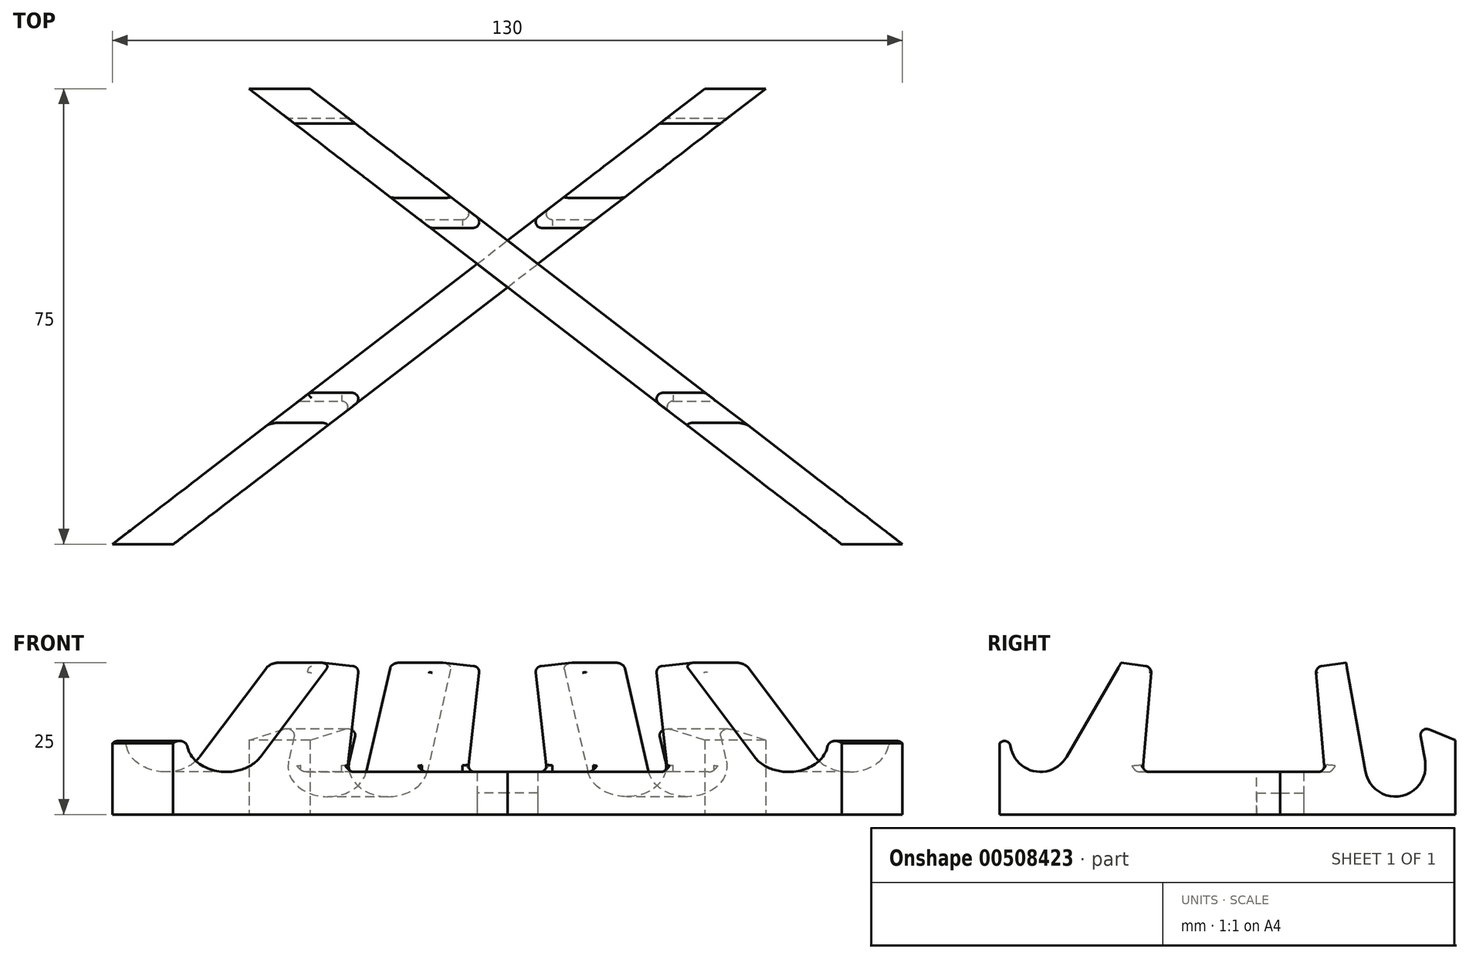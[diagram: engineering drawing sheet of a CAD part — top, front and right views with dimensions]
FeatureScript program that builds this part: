
annotation { "Feature Type Name" : "Feature", "Feature Type Description" : "" }
export const myFeature = defineFeature(function(context is Context, id is Id, definition is map)
    precondition{}
    {
        {
            var Q0;
            Q0=qCreatedBy(makeId("Top.planeOp"),FACE);
            var sketch = newSketch(context, id + "F0", { "sketchPlane" : qUnion([Q0])});
            skLineSegment(sketch, "E0.bottom", {"start": v(-55, 0) * mm, "end": v(-65, 0) * mm});
            skLineSegment(sketch, "E0.top", {"start": v(42.5, 75) * mm, "end": v(32.5, 75) * mm});
            skLineSegment(sketch, "E0.left", {"start": v(-55, 0) * mm, "end": v(42.5, 75) * mm});
            skLineSegment(sketch, "E0.right", {"start": v(-65, 0) * mm, "end": v(32.5, 75) * mm});
            skLineSegment(sketch, "E1", {"start": v(0, -60.62) * mm, "end": v(0, 193.14) * mm, "construction": true});
            skPoint(sketch, "E2", {"position": v(0, 50) * mm});
            skLineSegment(sketch, "E3.MirrorCS", {"start": v(65, 0) * mm, "end": v(-32.5, 75) * mm});
            skLineSegment(sketch, "E4.MirrorCS", {"start": v(55, 0) * mm, "end": v(-42.5, 75) * mm});
            skLineSegment(sketch, "E5.MirrorCS", {"start": v(-42.5, 75) * mm, "end": v(-32.5, 75) * mm});
            skLineSegment(sketch, "E6.MirrorCS", {"start": v(55, 0) * mm, "end": v(65, 0) * mm});
            skSolve(sketch);
        }
        {
            var Q0;
            {var subQ0=sQuery(id+"F0.wireOp",EDGE,"E0.bottom");Q0=makeQuery(id+"F0.imprint","IMPRINT",FACE,{"disambiguationData":[TD([[makeQuery(id+"F0.imprint","IMPRINT",EDGE,{"derivedFrom":subQ0}),-1.0]])]});}
            var Q1;
            {var subQ0=sQuery(id+"F0.wireOp",EDGE,"E4.MirrorCS");var subQ1=sQuery(id+"F0.wireOp",EDGE,"E0.left");var subQ2=makeQuery(id+"F0.imprint","INTERSECT",VERTEX,{"derivedFrom":[subQ1,subQ0]});Q1=makeQuery(id+"F0.imprint","IMPRINT",FACE,{"disambiguationData":[TD([[makeQuery(id+"F0.imprint","IMPRINT",EDGE,{"disambiguationData":[TD([[subQ2,-1.0]])],"derivedFrom":subQ1}),1.0]])]});}
            var Q2;
            {var subQ0=sQuery(id+"F0.wireOp",EDGE,"E0.top");Q2=makeQuery(id+"F0.imprint","IMPRINT",FACE,{"disambiguationData":[TD([[makeQuery(id+"F0.imprint","IMPRINT",EDGE,{"derivedFrom":subQ0}),1.0]])]});}
            extrude(context, id + "F1", {"entities" : qUnion([Q0, Q1, Q2]), "depth" : 25 * mm});
        }
        {
            var Q0;
            {var subQ5=sQuery(id+"F0.wireOp",EDGE,"E6.MirrorCS");Q0=makeQuery(id+"F0.imprint","IMPRINT",FACE,{"disambiguationData":[TD([[makeQuery(id+"F0.imprint","IMPRINT",EDGE,{"derivedFrom":subQ5}),1.0]])]});}
            var Q1;
            {var subQ5=sQuery(id+"F0.wireOp",EDGE,"E5.MirrorCS");Q1=makeQuery(id+"F0.imprint","IMPRINT",FACE,{"disambiguationData":[TD([[makeQuery(id+"F0.imprint","IMPRINT",EDGE,{"derivedFrom":subQ5}),-1.0]])]});}
            var Q2;
            {var subQ0=sQuery(id+"F0.wireOp",EDGE,"E4.MirrorCS");var subQ1=sQuery(id+"F0.wireOp",EDGE,"E0.left");var subQ2=makeQuery(id+"F0.imprint","INTERSECT",VERTEX,{"derivedFrom":[subQ1,subQ0]});Q2=makeQuery(id+"F0.imprint","IMPRINT",FACE,{"disambiguationData":[TD([[makeQuery(id+"F0.imprint","IMPRINT",EDGE,{"disambiguationData":[TD([[subQ2,-1.0]])],"derivedFrom":subQ1}),1.0]])]});}
            extrude(context, id + "F2", {"entities" : qUnion([Q0, Q1, Q2]), "depth" : 25 * mm});
        }
        {
            var Q0;
            Q0=qCreatedBy(makeId("Right.planeOp"),FACE);
            var sketch = newSketch(context, id + "F3", { "sketchPlane" : qUnion([Q0])});
            skLineSegment(sketch, "E7", {"start": v(3.4, 16.23) * mm, "end": v(0, 11.72) * mm});
            skLineSegment(sketch, "E8", {"start": v(3.4, 16.23) * mm, "end": v(2.4, 14.5) * mm});
            skLineSegment(sketch, "E9", {"start": v(2.4, 14.5) * mm, "end": v(11.05, 9.5) * mm, "construction": true});
            skLineSegment(sketch, "E10", {"start": v(11.05, 9.5) * mm, "end": v(20, 25) * mm});
            skLineSegment(sketch, "E11", {"start": v(75, 7) * mm, "end": v(75, 25) * mm, "construction": true});
            skLineSegment(sketch, "E12", {"start": v(75, 25) * mm, "end": v(0, 25) * mm});
            skLineSegment(sketch, "E13", {"start": v(0, 25) * mm, "end": v(0, 11.72) * mm});
            skArc(sketch, "E14", {"start": v(2.4, 14.5) * mm, "mid": v(4.22, 7.67) * mm, "end": v(11.05, 9.5) * mm});
            skLineSegment(sketch, "E15", {"start": v(20, 25) * mm, "end": v(25, 24.3) * mm});
            skLineSegment(sketch, "E16", {"start": v(25, 24.3) * mm, "end": v(23.49, 7) * mm});
            skLineSegment(sketch, "E17", {"start": v(23.49, 7) * mm, "end": v(75, 7) * mm, "construction": true});
            skLineSegment(sketch, "E18", {"start": v(57, 25) * mm, "end": v(52, 24.3) * mm});
            skLineSegment(sketch, "E19", {"start": v(52, 24.3) * mm, "end": v(53.51, 7) * mm});
            skLineSegment(sketch, "E20", {"start": v(23.49, 7) * mm, "end": v(53.51, 7) * mm});
            skLineSegment(sketch, "E21", {"start": v(57, 25) * mm, "end": v(60.16, 7.06) * mm});
            skArc(sketch, "E22", {"start": v(60.16, 7.06) * mm, "mid": v(65.96, 3) * mm, "end": v(70.01, 8.8) * mm});
            skLineSegment(sketch, "E23", {"start": v(70.01, 8.8) * mm, "end": v(60.16, 7.06) * mm, "construction": true});
            skLineSegment(sketch, "E24", {"start": v(75, 25) * mm, "end": v(75, 12.21) * mm});
            skLineSegment(sketch, "E25", {"start": v(75, 12.21) * mm, "end": v(68.97, 14.7) * mm});
            skLineSegment(sketch, "E26", {"start": v(68.97, 14.7) * mm, "end": v(70.01, 8.8) * mm});
            skSolve(sketch);
        }
        {
            var Q0;
            Q0=qSketchRegion(id+"F3",true);
            extrude(context, id + "F4", {"entities" : qUnion([Q0]), "operationType" : NewBodyOperationType.REMOVE, "endBound" : BoundingType.THROUGH_ALL, "depth" : 25 * mm, "hasSecondDirection" : true, "secondDirectionBound" : BoundingType.THROUGH_ALL, "secondDirectionOppositeDirection" : true, "secondDirectionDepth" : 25 * mm});
        }
        {
            var Q0;
            {var subQ0=sQuery(id+"F0.wireOp",EDGE,"E4.MirrorCS");var subQ1=sQuery(id+"F0.wireOp",EDGE,"E0.left");var subQ2=makeQuery(id+"F0.imprint","INTERSECT",VERTEX,{"derivedFrom":[subQ1,subQ0]});Q0=makeQuery(id+"F0.imprint","IMPRINT",FACE,{"disambiguationData":[TD([[makeQuery(id+"F0.imprint","IMPRINT",EDGE,{"disambiguationData":[TD([[subQ2,-1.0]])],"derivedFrom":subQ1}),1.0]])]});}
            extrude(context, id + "F5", {"entities" : qUnion([Q0]), "operationType" : NewBodyOperationType.REMOVE, "depth" : 3.5 * mm});
        }
        {
            var Q0;
            Q0=makeQuery(id+"F2.opExtrude","SWEPT_BODY",BODY,{"disambiguationData":[OSD([sQuery(id+"F0.wireOp",EDGE,"E3.MirrorCS"),sQuery(id+"F0.wireOp",EDGE,"E4.MirrorCS"),sQuery(id+"F0.wireOp",EDGE,"E5.MirrorCS"),sQuery(id+"F0.wireOp",EDGE,"E6.MirrorCS")])]});
            var Q1;
            Q1=makeQuery(id+"F1.opExtrude","SWEPT_BODY",BODY,{"disambiguationData":[OSD([sQuery(id+"F0.wireOp",EDGE,"E0.bottom"),sQuery(id+"F0.wireOp",EDGE,"E0.top"),sQuery(id+"F0.wireOp",EDGE,"E0.left"),sQuery(id+"F0.wireOp",EDGE,"E0.right")])]});
            booleanBodies(context, id + "F6", {"operationType" : BooleanOperationType.SUBTRACTION, "tools" : qUnion([Q0]), "targets" : qUnion([Q1]), "keepTools" : true});
        }
        {
            var Q0;
            Q0=makeQuery(id+"F4.boolean.opBoolean","INTERSECT",EDGE,{"derivedFrom":[makeQuery(id+"F1.opExtrude","SWEPT_FACE",FACE,{"disambiguationData":[OSD([sQuery(id+"F0.wireOp",EDGE,"E0.left")])]}),makeQuery(id+"F4.opExtrude","SWEPT_FACE",FACE,{"disambiguationData":[OSD([sQuery(id+"F3.wireOp",EDGE,"E16")])]})]});
            var Q1;
            Q1=makeQuery(id+"F4.boolean.opBoolean","INTERSECT",EDGE,{"derivedFrom":[makeQuery(id+"F2.opExtrude","SWEPT_FACE",FACE,{"disambiguationData":[OSD([sQuery(id+"F0.wireOp",EDGE,"E4.MirrorCS")])]}),makeQuery(id+"F4.opExtrude","SWEPT_FACE",FACE,{"disambiguationData":[OSD([sQuery(id+"F3.wireOp",EDGE,"E16")])]})]});
            var Q2;
            Q2=makeQuery(id+"F4.boolean.opBoolean","INTERSECT",EDGE,{"derivedFrom":[makeQuery(id+"F1.opExtrude","SWEPT_FACE",FACE,{"disambiguationData":[OSD([sQuery(id+"F0.wireOp",EDGE,"E0.right")])]}),makeQuery(id+"F4.opExtrude","SWEPT_FACE",FACE,{"disambiguationData":[OSD([sQuery(id+"F3.wireOp",EDGE,"E16")])]})]});
            var Q3;
            Q3=makeQuery(id+"F4.boolean.opBoolean","INTERSECT",EDGE,{"derivedFrom":[makeQuery(id+"F2.opExtrude","SWEPT_FACE",FACE,{"disambiguationData":[OSD([sQuery(id+"F0.wireOp",EDGE,"E3.MirrorCS")])]}),makeQuery(id+"F4.opExtrude","SWEPT_FACE",FACE,{"disambiguationData":[OSD([sQuery(id+"F3.wireOp",EDGE,"E16")])]})]});
            var Q4;
            Q4=makeQuery(id+"F4.boolean.opBoolean","INTERSECT",EDGE,{"derivedFrom":[makeQuery(id+"F2.opExtrude","SWEPT_FACE",FACE,{"disambiguationData":[OSD([sQuery(id+"F0.wireOp",EDGE,"E4.MirrorCS")])]}),makeQuery(id+"F4.opExtrude","SWEPT_FACE",FACE,{"disambiguationData":[OSD([sQuery(id+"F3.wireOp",EDGE,"E19")])]})]});
            var Q5;
            Q5=makeQuery(id+"F4.boolean.opBoolean","INTERSECT",EDGE,{"derivedFrom":[makeQuery(id+"F2.opExtrude","SWEPT_FACE",FACE,{"disambiguationData":[OSD([sQuery(id+"F0.wireOp",EDGE,"E3.MirrorCS")])]}),makeQuery(id+"F4.opExtrude","SWEPT_FACE",FACE,{"disambiguationData":[OSD([sQuery(id+"F3.wireOp",EDGE,"E19")])]})]});
            var Q6;
            Q6=makeQuery(id+"F4.boolean.opBoolean","INTERSECT",EDGE,{"derivedFrom":[makeQuery(id+"F1.opExtrude","SWEPT_FACE",FACE,{"disambiguationData":[OSD([sQuery(id+"F0.wireOp",EDGE,"E0.right")])]}),makeQuery(id+"F4.opExtrude","SWEPT_FACE",FACE,{"disambiguationData":[OSD([sQuery(id+"F3.wireOp",EDGE,"E19")])]})]});
            var Q7;
            Q7=makeQuery(id+"F4.boolean.opBoolean","INTERSECT",EDGE,{"derivedFrom":[makeQuery(id+"F1.opExtrude","SWEPT_FACE",FACE,{"disambiguationData":[OSD([sQuery(id+"F0.wireOp",EDGE,"E0.left")])]}),makeQuery(id+"F4.opExtrude","SWEPT_FACE",FACE,{"disambiguationData":[OSD([sQuery(id+"F3.wireOp",EDGE,"E19")])]})]});
            fillet(context, id + "F7", {"entities" : qUnion([Q0, Q1, Q2, Q3, Q4, Q5, Q6, Q7]), "radius" : 1 * mm, "tangentPropagation" : true, "allowEdgeOverflow" : false});
        }
        {
            var Q0;
            {var subQ0=sQuery(id+"F0.wireOp",EDGE,"E0.left");var subQ1=sQuery(id+"F0.wireOp",EDGE,"E0.bottom");var subQ4=sQuery(id+"F3.wireOp",EDGE,"E8");var subQ5=sQuery(id+"F3.wireOp",EDGE,"E7");Q0=makeQuery(id+"F4.boolean.opBoolean","COPY",EDGE,{"disambiguationData":[TD([makeQuery(id+"F1.opExtrude","SWEPT_FACE",FACE,{"disambiguationData":[OSD([subQ0]),TDD([makeQuery(id+"F0.imprint","IMPRINT",EDGE,{"disambiguationData":[TD([[makeQuery(id+"F0.imprint","INTERSECT",VERTEX,{"derivedFrom":[subQ1,subQ0]}),-1.0]])],"derivedFrom":subQ0})])]})])],"derivedFrom":makeQuery(id+"F4.opExtrude","SWEPT_EDGE",EDGE,{"disambiguationData":[OSD([subQ5,subQ4])]})});}
            var Q1;
            {var subQ0=sQuery(id+"F0.wireOp",EDGE,"E6.MirrorCS");var subQ1=sQuery(id+"F0.wireOp",EDGE,"E3.MirrorCS");var subQ3=sQuery(id+"F3.wireOp",EDGE,"E7");var subQ5=sQuery(id+"F3.wireOp",EDGE,"E8");Q1=makeQuery(id+"F4.boolean.opBoolean","COPY",EDGE,{"disambiguationData":[TD([makeQuery(id+"F1.opExtrude","SWEPT_FACE",FACE,{"disambiguationData":[OSD([subQ1]),TDD([makeQuery(id+"F0.imprint","IMPRINT",EDGE,{"disambiguationData":[TD([[makeQuery(id+"F0.imprint","INTERSECT",VERTEX,{"derivedFrom":[subQ1,subQ0]}),-1.0]])],"derivedFrom":subQ1})])]})])],"derivedFrom":makeQuery(id+"F4.opExtrude","SWEPT_EDGE",EDGE,{"disambiguationData":[OSD([subQ3,subQ5])]})});}
            var Q2;
            {var subQ0=sQuery(id+"F3.wireOp",EDGE,"E7");Q2=makeQuery(id+"F4.boolean.opBoolean","COPY",EDGE,{"disambiguationData":[topologyDisambiguationEdgeConnected([makeQuery(id+"F1.opExtrude","SWEPT_FACE",FACE,{"disambiguationData":[OSD([sQuery(id+"F0.wireOp",EDGE,"E0.bottom")])]})])],"derivedFrom":makeQuery(id+"F4.opExtrude","SWEPT_EDGE",EDGE,{"disambiguationData":[OSD([subQ0,sQuery(id+"F3.wireOp",EDGE,"E13")])]})});}
            var Q3;
            {var subQ0=sQuery(id+"F3.wireOp",EDGE,"E7");Q3=makeQuery(id+"F4.boolean.opBoolean","COPY",EDGE,{"disambiguationData":[topologyDisambiguationEdgeConnected([makeQuery(id+"F1.opExtrude","SWEPT_FACE",FACE,{"disambiguationData":[OSD([sQuery(id+"F0.wireOp",EDGE,"E6.MirrorCS")])]})])],"derivedFrom":makeQuery(id+"F4.opExtrude","SWEPT_EDGE",EDGE,{"disambiguationData":[OSD([subQ0,sQuery(id+"F3.wireOp",EDGE,"E13")])]})});}
            var Q4;
            {var subQ0=sQuery(id+"F3.wireOp",EDGE,"E15");var subQ1=sQuery(id+"F3.wireOp",EDGE,"E12");var subQ2=sQuery(id+"F3.wireOp",EDGE,"E10");Q4=makeQuery(id+"F4.boolean.opBoolean","TWEAK_EDGE",EDGE,{"disambiguationData":[OD(0.0)],"derivedFrom":[makeQuery(id+"F4.opExtrude","SWEPT_EDGE",EDGE,{"disambiguationData":[OSD([subQ2,subQ1,subQ0]),ownerDisambiguation([makeQuery(id+"F3.imprint","IMPRINT",EDGE,{"derivedFrom":sQuery(id+"F3.wireOp",EDGE,"E7")})])]}),makeQuery(id+"F4.opExtrude","SWEPT_EDGE",EDGE,{"disambiguationData":[OSD([subQ2,subQ1,subQ0]),ownerDisambiguation([makeQuery(id+"F3.imprint","IMPRINT",EDGE,{"derivedFrom":sQuery(id+"F3.wireOp",EDGE,"E11")})])]})]});}
            var Q5;
            {var subQ0=sQuery(id+"F3.wireOp",EDGE,"E15");var subQ1=sQuery(id+"F3.wireOp",EDGE,"E12");var subQ2=sQuery(id+"F3.wireOp",EDGE,"E10");Q5=makeQuery(id+"F4.boolean.opBoolean","TWEAK_EDGE",EDGE,{"disambiguationData":[OD(1.0)],"derivedFrom":[makeQuery(id+"F4.opExtrude","SWEPT_EDGE",EDGE,{"disambiguationData":[OSD([subQ2,subQ1,subQ0]),ownerDisambiguation([makeQuery(id+"F3.imprint","IMPRINT",EDGE,{"derivedFrom":sQuery(id+"F3.wireOp",EDGE,"E7")})])]}),makeQuery(id+"F4.opExtrude","SWEPT_EDGE",EDGE,{"disambiguationData":[OSD([subQ2,subQ1,subQ0]),ownerDisambiguation([makeQuery(id+"F3.imprint","IMPRINT",EDGE,{"derivedFrom":sQuery(id+"F3.wireOp",EDGE,"E11")})])]})]});}
            var Q6;
            {var subQ0=sQuery(id+"F0.wireOp",EDGE,"E0.left");var subQ1=sQuery(id+"F0.wireOp",EDGE,"E0.bottom");var subQ4=sQuery(id+"F3.wireOp",EDGE,"E16");var subQ5=sQuery(id+"F3.wireOp",EDGE,"E15");Q6=makeQuery(id+"F4.boolean.opBoolean","COPY",EDGE,{"disambiguationData":[TD([makeQuery(id+"F1.opExtrude","SWEPT_FACE",FACE,{"disambiguationData":[OSD([subQ0]),TDD([makeQuery(id+"F0.imprint","IMPRINT",EDGE,{"disambiguationData":[TD([[makeQuery(id+"F0.imprint","INTERSECT",VERTEX,{"derivedFrom":[subQ1,subQ0]}),-1.0]])],"derivedFrom":subQ0})])]})])],"derivedFrom":makeQuery(id+"F4.opExtrude","SWEPT_EDGE",EDGE,{"disambiguationData":[OSD([subQ5,subQ4])]})});}
            var Q7;
            {var subQ0=sQuery(id+"F0.wireOp",EDGE,"E0.left");var subQ1=sQuery(id+"F0.wireOp",EDGE,"E0.bottom");var subQ4=sQuery(id+"F3.wireOp",EDGE,"E16");var subQ5=sQuery(id+"F3.wireOp",EDGE,"E17");Q7=makeQuery(id+"F4.boolean.opBoolean","COPY",EDGE,{"disambiguationData":[TD([makeQuery(id+"F1.opExtrude","SWEPT_FACE",FACE,{"disambiguationData":[OSD([subQ0]),TDD([makeQuery(id+"F0.imprint","IMPRINT",EDGE,{"disambiguationData":[TD([[makeQuery(id+"F0.imprint","INTERSECT",VERTEX,{"derivedFrom":[subQ1,subQ0]}),-1.0]])],"derivedFrom":subQ0})])]})])],"derivedFrom":makeQuery(id+"F4.opExtrude","SWEPT_EDGE",EDGE,{"disambiguationData":[OSD([subQ4,subQ5])]})});}
            var Q8;
            {var subQ0=sQuery(id+"F0.wireOp",EDGE,"E6.MirrorCS");var subQ1=sQuery(id+"F0.wireOp",EDGE,"E3.MirrorCS");var subQ4=sQuery(id+"F3.wireOp",EDGE,"E16");var subQ5=sQuery(id+"F3.wireOp",EDGE,"E17");Q8=makeQuery(id+"F4.boolean.opBoolean","COPY",EDGE,{"disambiguationData":[TD([makeQuery(id+"F1.opExtrude","SWEPT_FACE",FACE,{"disambiguationData":[OSD([subQ1]),TDD([makeQuery(id+"F0.imprint","IMPRINT",EDGE,{"disambiguationData":[TD([[makeQuery(id+"F0.imprint","INTERSECT",VERTEX,{"derivedFrom":[subQ1,subQ0]}),-1.0]])],"derivedFrom":subQ1})])]})])],"derivedFrom":makeQuery(id+"F4.opExtrude","SWEPT_EDGE",EDGE,{"disambiguationData":[OSD([subQ4,subQ5])]})});}
            var Q9;
            {var subQ0=sQuery(id+"F0.wireOp",EDGE,"E6.MirrorCS");var subQ1=sQuery(id+"F0.wireOp",EDGE,"E3.MirrorCS");var subQ4=sQuery(id+"F3.wireOp",EDGE,"E15");var subQ5=sQuery(id+"F3.wireOp",EDGE,"E16");Q9=makeQuery(id+"F4.boolean.opBoolean","COPY",EDGE,{"disambiguationData":[TD([makeQuery(id+"F1.opExtrude","SWEPT_FACE",FACE,{"disambiguationData":[OSD([subQ1]),TDD([makeQuery(id+"F0.imprint","IMPRINT",EDGE,{"disambiguationData":[TD([[makeQuery(id+"F0.imprint","INTERSECT",VERTEX,{"derivedFrom":[subQ1,subQ0]}),-1.0]])],"derivedFrom":subQ1})])]})])],"derivedFrom":makeQuery(id+"F4.opExtrude","SWEPT_EDGE",EDGE,{"disambiguationData":[OSD([subQ4,subQ5])]})});}
            var Q10;
            {var subQ0=sQuery(id+"F3.wireOp",EDGE,"E7");var subQ1=sQuery(id+"F3.wireOp",EDGE,"E8");Q10=makeQuery(id+"F4.boolean.opBoolean","COPY",EDGE,{"disambiguationData":[TD([makeQuery(id+"F2.opExtrude","SWEPT_FACE",FACE,{"disambiguationData":[OSD([sQuery(id+"F0.wireOp",EDGE,"E3.MirrorCS")])]})])],"derivedFrom":makeQuery(id+"F4.opExtrude","SWEPT_EDGE",EDGE,{"disambiguationData":[OSD([subQ0,subQ1])]})});}
            var Q11;
            {var subQ0=sQuery(id+"F3.wireOp",EDGE,"E15");var subQ1=sQuery(id+"F3.wireOp",EDGE,"E16");Q11=makeQuery(id+"F4.boolean.opBoolean","COPY",EDGE,{"disambiguationData":[TD([makeQuery(id+"F2.opExtrude","SWEPT_FACE",FACE,{"disambiguationData":[OSD([sQuery(id+"F0.wireOp",EDGE,"E3.MirrorCS")])]})])],"derivedFrom":makeQuery(id+"F4.opExtrude","SWEPT_EDGE",EDGE,{"disambiguationData":[OSD([subQ0,subQ1])]})});}
            var Q12;
            {var subQ0=sQuery(id+"F3.wireOp",EDGE,"E16");var subQ1=sQuery(id+"F3.wireOp",EDGE,"E17");Q12=makeQuery(id+"F4.boolean.opBoolean","COPY",EDGE,{"disambiguationData":[TD([makeQuery(id+"F2.opExtrude","SWEPT_FACE",FACE,{"disambiguationData":[OSD([sQuery(id+"F0.wireOp",EDGE,"E3.MirrorCS")])]})])],"derivedFrom":makeQuery(id+"F4.opExtrude","SWEPT_EDGE",EDGE,{"disambiguationData":[OSD([subQ0,subQ1])]})});}
            var Q13;
            {var subQ0=sQuery(id+"F3.wireOp",EDGE,"E19");var subQ1=sQuery(id+"F3.wireOp",EDGE,"E20");Q13=makeQuery(id+"F4.boolean.opBoolean","COPY",EDGE,{"disambiguationData":[TD([makeQuery(id+"F2.opExtrude","SWEPT_FACE",FACE,{"disambiguationData":[OSD([sQuery(id+"F0.wireOp",EDGE,"E3.MirrorCS")])]})])],"derivedFrom":makeQuery(id+"F4.opExtrude","SWEPT_EDGE",EDGE,{"disambiguationData":[OSD([subQ0,subQ1])]})});}
            var Q14;
            {var subQ0=sQuery(id+"F3.wireOp",EDGE,"E19");var subQ1=sQuery(id+"F3.wireOp",EDGE,"E20");Q14=makeQuery(id+"F4.boolean.opBoolean","COPY",EDGE,{"disambiguationData":[TD([makeQuery(id+"F1.opExtrude","SWEPT_FACE",FACE,{"disambiguationData":[OSD([sQuery(id+"F0.wireOp",EDGE,"E0.left")])]})])],"derivedFrom":makeQuery(id+"F4.opExtrude","SWEPT_EDGE",EDGE,{"disambiguationData":[OSD([subQ0,subQ1])]})});}
            var Q15;
            {var subQ0=makeQuery(id+"F1.opExtrude","SWEPT_FACE",FACE,{"disambiguationData":[OSD([sQuery(id+"F0.wireOp",EDGE,"E0.right")])]});var subQ1=makeQuery(id+"F4.opExtrude","SWEPT_FACE",FACE,{"disambiguationData":[OSD([sQuery(id+"F3.wireOp",EDGE,"E19")])]});Q15=makeQuery(id+"F7.opFillet","BLEND_EDGE",EDGE,{"blendedFrom":[makeQuery(id+"F4.boolean.opBoolean","INTERSECT",EDGE,{"derivedFrom":[subQ0,subQ1]}),makeQuery(id+"F4.boolean.opBoolean","COPY",FACE,{"disambiguationData":[TD([makeQuery(id+"F1.opExtrude","SWEPT_FACE",FACE,{"disambiguationData":[OSD([sQuery(id+"F0.wireOp",EDGE,"E0.left")])]})])],"derivedFrom":makeQuery(id+"F4.opExtrude","SWEPT_FACE",FACE,{"disambiguationData":[OSD([sQuery(id+"F3.wireOp",EDGE,"E18")])]})})],"blendedInto":[makeQuery(id+"F4.boolean.opBoolean","COPY",FACE,{"disambiguationData":[TD([makeQuery(id+"F1.opExtrude","SWEPT_FACE",FACE,{"disambiguationData":[OSD([sQuery(id+"F0.wireOp",EDGE,"E0.left")])]})])],"derivedFrom":makeQuery(id+"F4.opExtrude","SWEPT_FACE",FACE,{"disambiguationData":[OSD([sQuery(id+"F3.wireOp",EDGE,"E18")])]})})]});}
            var Q16;
            {var subQ0=makeQuery(id+"F2.opExtrude","SWEPT_FACE",FACE,{"disambiguationData":[OSD([sQuery(id+"F0.wireOp",EDGE,"E3.MirrorCS")])]});var subQ1=makeQuery(id+"F4.opExtrude","SWEPT_FACE",FACE,{"disambiguationData":[OSD([sQuery(id+"F3.wireOp",EDGE,"E19")])]});Q16=makeQuery(id+"F7.opFillet","BLEND_EDGE",EDGE,{"blendedFrom":[makeQuery(id+"F4.boolean.opBoolean","INTERSECT",EDGE,{"derivedFrom":[subQ0,subQ1]}),makeQuery(id+"F4.boolean.opBoolean","COPY",FACE,{"disambiguationData":[TD([subQ0])],"derivedFrom":makeQuery(id+"F4.opExtrude","SWEPT_FACE",FACE,{"disambiguationData":[OSD([sQuery(id+"F3.wireOp",EDGE,"E18")])]})})],"blendedInto":[makeQuery(id+"F4.boolean.opBoolean","COPY",FACE,{"disambiguationData":[TD([subQ0])],"derivedFrom":makeQuery(id+"F4.opExtrude","SWEPT_FACE",FACE,{"disambiguationData":[OSD([sQuery(id+"F3.wireOp",EDGE,"E18")])]})})]});}
            var Q17;
            {var subQ0=sQuery(id+"F3.wireOp",EDGE,"E25");Q17=makeQuery(id+"F4.boolean.opBoolean","COPY",EDGE,{"disambiguationData":[topologyDisambiguationEdgeConnected([makeQuery(id+"F1.opExtrude","SWEPT_FACE",FACE,{"disambiguationData":[OSD([sQuery(id+"F0.wireOp",EDGE,"E0.top")])]})])],"derivedFrom":makeQuery(id+"F4.opExtrude","SWEPT_EDGE",EDGE,{"disambiguationData":[OSD([sQuery(id+"F3.wireOp",EDGE,"E24"),subQ0])]})});}
            var Q18;
            {var subQ0=sQuery(id+"F3.wireOp",EDGE,"E25");var subQ1=sQuery(id+"F3.wireOp",EDGE,"E26");Q18=makeQuery(id+"F4.boolean.opBoolean","COPY",EDGE,{"disambiguationData":[TD([makeQuery(id+"F1.opExtrude","SWEPT_FACE",FACE,{"disambiguationData":[OSD([sQuery(id+"F0.wireOp",EDGE,"E0.left")])]})])],"derivedFrom":makeQuery(id+"F4.opExtrude","SWEPT_EDGE",EDGE,{"disambiguationData":[OSD([subQ0,subQ1])]})});}
            var Q19;
            {var subQ0=sQuery(id+"F3.wireOp",EDGE,"E25");Q19=makeQuery(id+"F4.boolean.opBoolean","COPY",EDGE,{"disambiguationData":[topologyDisambiguationEdgeConnected([makeQuery(id+"F2.opExtrude","SWEPT_FACE",FACE,{"disambiguationData":[OSD([sQuery(id+"F0.wireOp",EDGE,"E5.MirrorCS")])]})])],"derivedFrom":makeQuery(id+"F4.opExtrude","SWEPT_EDGE",EDGE,{"disambiguationData":[OSD([sQuery(id+"F3.wireOp",EDGE,"E24"),subQ0])]})});}
            var Q20;
            {var subQ0=sQuery(id+"F3.wireOp",EDGE,"E25");var subQ1=sQuery(id+"F3.wireOp",EDGE,"E26");Q20=makeQuery(id+"F4.boolean.opBoolean","COPY",EDGE,{"disambiguationData":[TD([makeQuery(id+"F2.opExtrude","SWEPT_FACE",FACE,{"disambiguationData":[OSD([sQuery(id+"F0.wireOp",EDGE,"E3.MirrorCS")])]})])],"derivedFrom":makeQuery(id+"F4.opExtrude","SWEPT_EDGE",EDGE,{"disambiguationData":[OSD([subQ0,subQ1])]})});}
            fillet(context, id + "F8", {"entities" : qUnion([Q0, Q1, Q2, Q3, Q4, Q5, Q6, Q7, Q8, Q9, Q10, Q11, Q12, Q13, Q14, Q15, Q16, Q17, Q18, Q19, Q20]), "radius" : 1 * mm, "tangentPropagation" : true, "allowEdgeOverflow" : false});
        }
    });
